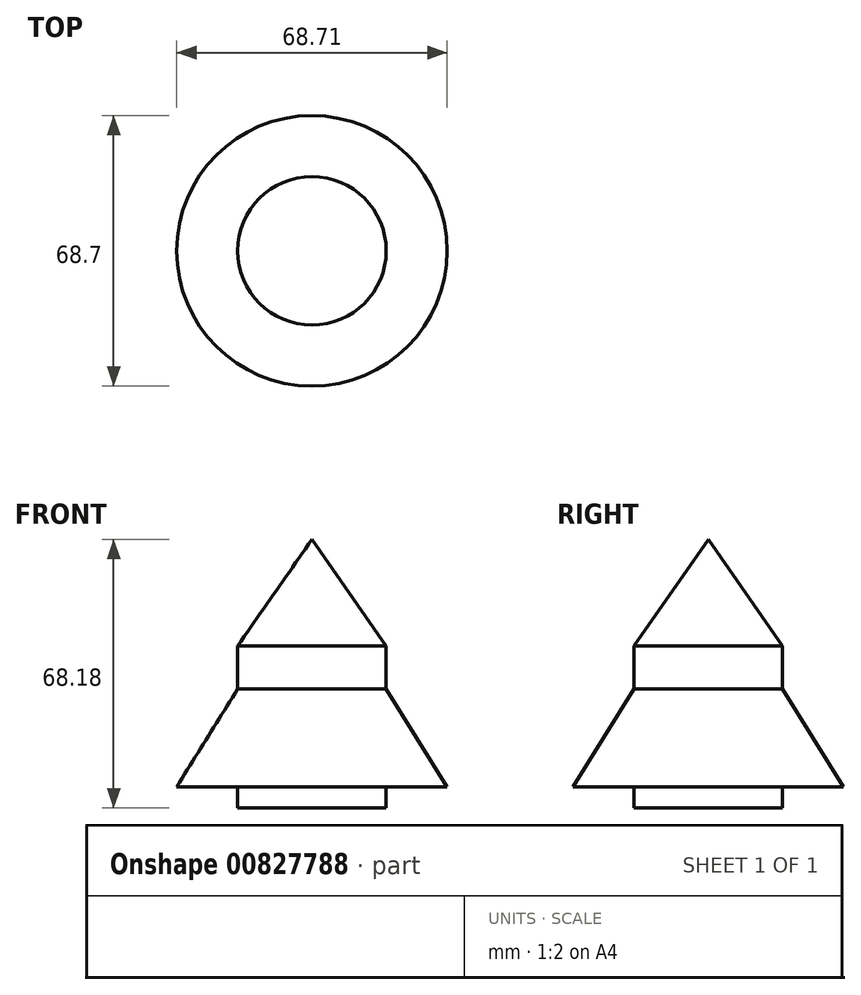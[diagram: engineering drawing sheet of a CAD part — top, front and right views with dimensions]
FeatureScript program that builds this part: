
annotation { "Feature Type Name" : "Feature", "Feature Type Description" : "" }
export const myFeature = defineFeature(function(context is Context, id is Id, definition is map)
    precondition{}
    {
        {
            var Q0;
            Q0=qCreatedBy(makeId("Front.planeOp"),FACE);
            var sketch = newSketch(context, id + "F0", { "sketchPlane" : qUnion([Q0])});
            skLineSegment(sketch, "E0", {"start": v(-51.7, 41.12) * mm, "end": v(-51.7, 14.09) * mm});
            skLineSegment(sketch, "E1", {"start": v(-51.7, 14.09) * mm, "end": v(-32.83, 14.09) * mm});
            skLineSegment(sketch, "E2", {"start": v(-32.83, 14.09) * mm, "end": v(-51.7, 41.12) * mm});
            skSolve(sketch);
        }
        {
            var Q0;
            Q0=qCreatedBy(makeId("Front.planeOp"),FACE);
            var sketch = newSketch(context, id + "F1", { "sketchPlane" : qUnion([Q0])});
            skLineSegment(sketch, "E3", {"start": v(-51.7, 40.87) * mm, "end": v(-51.7, 13.58) * mm});
            skSolve(sketch);
        }
        {
            var Q0;
            Q0=makeQuery(id+"F0.imprint","IMPRINT",FACE,{"disambiguationData":[TD([[makeQuery(id+"F0.imprint","IMPRINT",EDGE,{"derivedFrom":sQuery(id+"F0.wireOp",EDGE,"E0")}),1.0]])]});
            var Q1;
            Q1=sQuery(id+"F1.wireOp",EDGE,"E3");
            revolve(context, id + "F2", {"surfaceOperationType" : NewSurfaceOperationType.NEW, "entities" : qUnion([Q0]), "axis" : qUnion([Q1]), "revolveType" : RevolveType.FULL});
        }
        {
            var Q0;
            Q0=makeQuery(id+"F2.opRevolve","SWEPT_FACE",FACE,{"disambiguationData":[OSD([sQuery(id+"F0.wireOp",EDGE,"E1")])]});
            var sketch = newSketch(context, id + "F3", { "sketchPlane" : qUnion([Q0])});
            skCircle(sketch, "E4.0", {"center": v(-51.7, 0) * mm, "radius": 18.87 * mm});
            skSolve(sketch);
        }
        {
            var Q0;
            Q0=makeQuery(id+"F3.imprint","IMPRINT",FACE,{"disambiguationData":[TD([[makeQuery(id+"F3.imprint","IMPRINT",EDGE,{"derivedFrom":sQuery(id+"F3.wireOp",EDGE,"E4.0")}),-1.0]])]});
            extrude(context, id + "F4", {"entities" : qUnion([Q0]), "operationType" : NewBodyOperationType.ADD, "depth" : 41.15 * mm, "offsetDistance" : 25.4 * mm});
        }
        {
            var Q0;
            Q0=qCreatedBy(makeId("Front.planeOp"),FACE);
            var sketch = newSketch(context, id + "F5", { "sketchPlane" : qUnion([Q0])});
            skLineSegment(sketch, "E5", {"start": v(-67.71, 7.75) * mm, "end": v(-86.06, -21.69) * mm});
            skLineSegment(sketch, "E6", {"start": v(-86.06, -21.69) * mm, "end": v(-67.94, -21.69) * mm});
            skLineSegment(sketch, "E7.0", {"start": v(-70.58, -27.06) * mm, "end": v(-32.83, -27.06) * mm});
            skPoint(sketch, "E8", {"position": v(-51.7, -27.06) * mm});
            skLineSegment(sketch, "E9", {"start": v(-51.7, -27.06) * mm, "end": v(-51.7, 52.9) * mm});
            skLineSegment(sketch, "E10", {"start": v(-67.71, 7.75) * mm, "end": v(-67.94, -21.69) * mm});
            skSolve(sketch);
        }
        {
            var Q0;
            Q0=makeQuery(id+"F5.imprint","IMPRINT",FACE,{"disambiguationData":[TD([[makeQuery(id+"F5.imprint","IMPRINT",EDGE,{"derivedFrom":sQuery(id+"F5.wireOp",EDGE,"E5")}),1.0]])]});
            var Q1;
            Q1=sQuery(id+"F5.wireOp",EDGE,"E9");
            revolve(context, id + "F6", {"operationType" : NewBodyOperationType.ADD, "surfaceOperationType" : NewSurfaceOperationType.NEW, "entities" : qUnion([Q0]), "axis" : qUnion([Q1]), "revolveType" : RevolveType.FULL});
        }
    });
